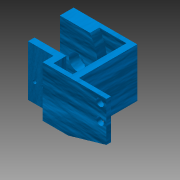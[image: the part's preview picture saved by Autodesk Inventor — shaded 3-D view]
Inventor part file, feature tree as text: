
AUTODESK INVENTOR PART (.ipt)
format: ipt  version: 2015 (Build 190159000, 159)  size: 214,016 bytes
history: native  units: in
note: dims shown in document units (in); Inventor stores cm internally (conversion verified against a paired STEP export)
features: sketch x10, extrude x7, hole x3
ambient origin geometry x8: Origin, YZ Plane, XZ Plane, XY Plane, X Axis, Y Axis, Z Axis, Center Point
bodies: Solid1 (feature_tree)
feature tree (20):
  extrude  "Extrusion1"  Depth=0.9843in
  extrude  "Extrusion2"  Depth=1.0in
  extrude  "Extrusion3"  Depth=1.0in TaperAngle=0.0deg
  hole  "Hole1"  [1 undecoded]
  extrude  "Extrusion4"  Depth=1.3in
  hole  "Hole2"  [1 undecoded]
  extrude  "Extrusion5"  Depth=0.1in
  extrude  "Extrusion6"  Depth=0.6in
  extrude  "Extrusion7"  Depth=0.15in TaperAngle=0.0deg
  hole  "Hole3"  [1 undecoded]
  sketch  "Sketch1"  dims[d1=0.07in d2=0.9843in]
  sketch  "Sketch2"  dims[d3=0.07in d5=1.0in]
  sketch  "Sketch3"  dims[d6=0.1in d7=1.0in d8=0.0in]
  sketch  "Sketch4"  dims[d9=1.9685in d10=0.1457in d11=0.0in]
  sketch  "Sketch5"  dims[d12=0.5079in d13=1.3in]
  sketch  "Sketch6"  dims[d14=3.0in d15=0.0in d16=0.273in]
  sketch  "Sketch7"  dims[d17=0.1in d18=0.2559in]
  sketch  "Sketch8"  dims[d19=0.1181in d20=0.75in d21=0.375in d22=0.25in d23=0.5635in d24=1.0in d25=0.8108in d26=0.6in]
  sketch  "Sketch9"  dims[d28=0.25in d29=0.15in d30=0.0in]
  sketch  "Sketch10"  dims[d31=0.07in d32=0.0591in d33=0.75in d34=0.375in d35=0.25in d36=0.5635in d37=1.0in d38=0.8108in d39=0.4in d40=0.0in d41=0.2in d42=0.0in d43=0.1in d44=0.1in d45=0.4in d46=0.0in d47=0.07in d48=0.33in d49=0.5in d50=0.0591in d51=0.75in d52=0.375in d53=0.25in d54=0.5635in d55=1.0in d56=0.8108in]
note: 3 required parameter values undecoded (feature->parameter linkage not recoverable at this tier; creation-order binding heuristic only, values carry confidence <= 0.55)
